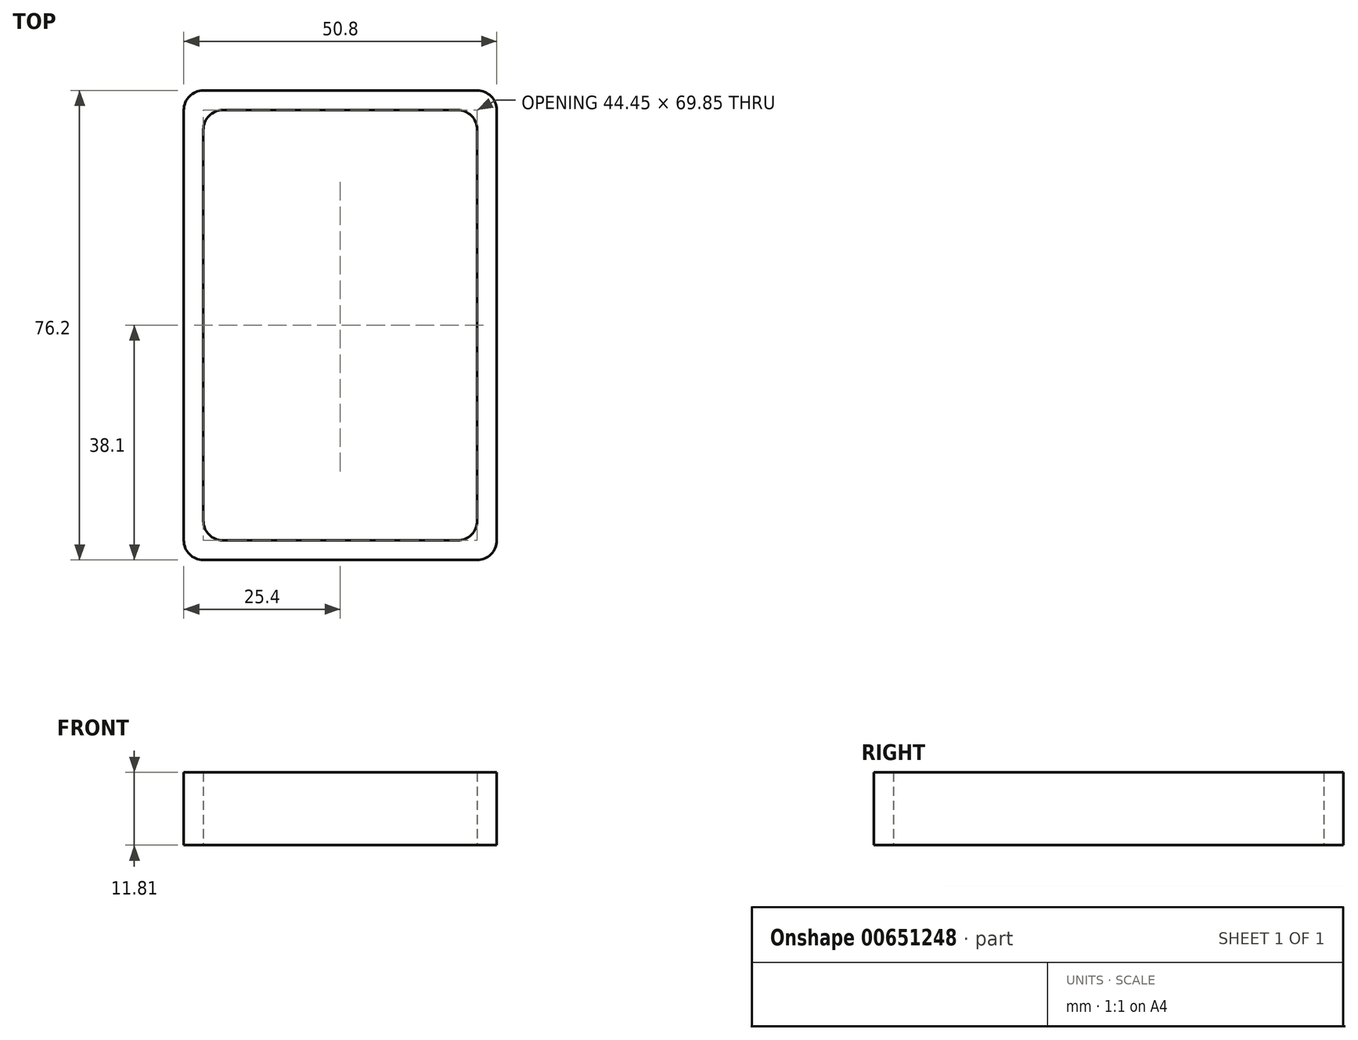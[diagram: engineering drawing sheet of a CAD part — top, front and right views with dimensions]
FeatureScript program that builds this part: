
annotation { "Feature Type Name" : "Feature", "Feature Type Description" : "" }
export const myFeature = defineFeature(function(context is Context, id is Id, definition is map)
    precondition{}
    {
        {
            var Q0;
            Q0=qCreatedBy(makeId("Top.planeOp"),FACE);
            var sketch = newSketch(context, id + "F0", { "sketchPlane" : qUnion([Q0])});
            skLineSegment(sketch, "E0.bottom", {"start": v(-25.4, 38.1) * mm, "end": v(25.4, 38.1) * mm});
            skLineSegment(sketch, "E0.top", {"start": v(-25.4, -38.1) * mm, "end": v(25.4, -38.1) * mm});
            skLineSegment(sketch, "E0.left", {"start": v(-25.4, 38.1) * mm, "end": v(-25.4, -38.1) * mm});
            skLineSegment(sketch, "E0.right", {"start": v(25.4, 38.1) * mm, "end": v(25.4, -38.1) * mm});
            skPoint(sketch, "E0.middle", {"position": v(0, 0) * mm});
            skLineSegment(sketch, "E1.bottom", {"start": v(-22.23, 34.93) * mm, "end": v(22.22, 34.93) * mm});
            skLineSegment(sketch, "E1.top", {"start": v(-22.23, -34.93) * mm, "end": v(22.22, -34.93) * mm});
            skLineSegment(sketch, "E1.left", {"start": v(-22.23, 34.93) * mm, "end": v(-22.23, -34.93) * mm});
            skLineSegment(sketch, "E1.right", {"start": v(22.22, 34.93) * mm, "end": v(22.22, -34.93) * mm});
            skSolve(sketch);
        }
        {
            assignVariable(context, id + "F1", {"name" : "Length", "anyValue" : 300 / 25.4});
        }
        {
            var Q0;
            Q0=makeQuery(id+"F0.imprint","IMPRINT",FACE,{"disambiguationData":[TD([[makeQuery(id+"F0.imprint","IMPRINT",EDGE,{"derivedFrom":sQuery(id+"F0.wireOp",EDGE,"E0.bottom")}),-1.0]])]});
            extrude(context, id + "F2", {"entities" : qUnion([Q0]), "depth" : (getVariable(context, 'Length')) * mm, "offsetDistance" : 25.4 * mm});
        }
        {
            var Q0;
            Q0=makeQuery(id+"F2.opExtrude","SWEPT_EDGE",EDGE,{"disambiguationData":[OSD([sQuery(id+"F0.wireOp",EDGE,"E1.bottom"),sQuery(id+"F0.wireOp",EDGE,"E1.left")])]});
            var Q1;
            Q1=makeQuery(id+"F2.opExtrude","SWEPT_EDGE",EDGE,{"disambiguationData":[OSD([sQuery(id+"F0.wireOp",EDGE,"E1.bottom"),sQuery(id+"F0.wireOp",EDGE,"E1.right")])]});
            var Q2;
            Q2=makeQuery(id+"F2.opExtrude","SWEPT_EDGE",EDGE,{"disambiguationData":[OSD([sQuery(id+"F0.wireOp",EDGE,"E1.top"),sQuery(id+"F0.wireOp",EDGE,"E1.right")])]});
            var Q3;
            Q3=makeQuery(id+"F2.opExtrude","SWEPT_EDGE",EDGE,{"disambiguationData":[OSD([sQuery(id+"F0.wireOp",EDGE,"E1.top"),sQuery(id+"F0.wireOp",EDGE,"E1.left")])]});
            var Q4;
            Q4=makeQuery(id+"F2.opExtrude","SWEPT_EDGE",EDGE,{"disambiguationData":[OSD([sQuery(id+"F0.wireOp",EDGE,"E0.bottom"),sQuery(id+"F0.wireOp",EDGE,"E0.right")])]});
            var Q5;
            Q5=makeQuery(id+"F2.opExtrude","SWEPT_EDGE",EDGE,{"disambiguationData":[OSD([sQuery(id+"F0.wireOp",EDGE,"E0.bottom"),sQuery(id+"F0.wireOp",EDGE,"E0.left")])]});
            var Q6;
            Q6=makeQuery(id+"F2.opExtrude","SWEPT_EDGE",EDGE,{"disambiguationData":[OSD([sQuery(id+"F0.wireOp",EDGE,"E0.top"),sQuery(id+"F0.wireOp",EDGE,"E0.right")])]});
            var Q7;
            Q7=makeQuery(id+"F2.opExtrude","SWEPT_EDGE",EDGE,{"disambiguationData":[OSD([sQuery(id+"F0.wireOp",EDGE,"E0.top"),sQuery(id+"F0.wireOp",EDGE,"E0.left")])]});
            fillet(context, id + "F3", {"entities" : qUnion([Q0, Q1, Q2, Q3, Q4, Q5, Q6, Q7]), "radius" : 3.17 * mm, "tangentPropagation" : true, "allowEdgeOverflow" : false});
        }
    });
